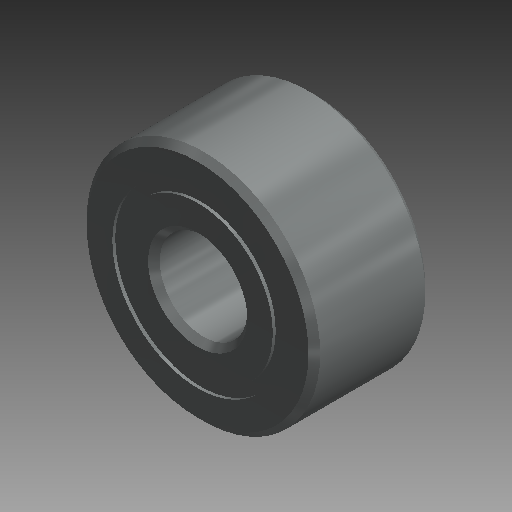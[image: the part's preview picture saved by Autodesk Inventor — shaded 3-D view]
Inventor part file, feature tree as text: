
AUTODESK INVENTOR PART (.ipt)
format: ipt  version: 2019 (Build 230136000, 136)  size: 577,536 bytes
history: native  units: mm (DEFAULTED — no unit token found)
features: other x11, revolve x5
ambient origin geometry x8: Origin, YZ Plane, XZ Plane, XY Plane, X Axis, Y Axis, Z Axis, Center Point
bodies: Solid1 (feature_tree), Solid2 (feature_tree), Solid3 (feature_tree), Solid4 (feature_tree), Solid5 (feature_tree), Solid6 (feature_tree), Solid7 (feature_tree), Solid8 (feature_tree), Solid9 (feature_tree), Solid10 (feature_tree), Solid11 (feature_tree), Solid12 (feature_tree), Solid13 (feature_tree), Solid14 (feature_tree), Solid15 (feature_tree), Solid16 (feature_tree)
feature tree (16):
  revolve  "Revolve1"  [1 undecoded]
  revolve  "Revolve3"  [1 undecoded]
  revolve  "Revolve4"  [1 undecoded]
  other  "CirPattern1[1]"
  other  "CirPattern1[2]"
  other  "CirPattern1[3]"
  other  "CirPattern1[4]"
  other  "CirPattern1[5]"
  other  "CirPattern1[6]"
  other  "CirPattern1[7]"
  other  "CirPattern1[8]"
  other  "CirPattern1[9]"
  other  "CirPattern1[10]"
  other  "CirPattern1[11]"
  revolve  "Revolve5[1]"  [1 undecoded]
  revolve  "Revolve5[2]"  [1 undecoded]
note: 5 required parameter values undecoded (feature->parameter linkage not recoverable at this tier; creation-order binding heuristic only, values carry confidence <= 0.55)
